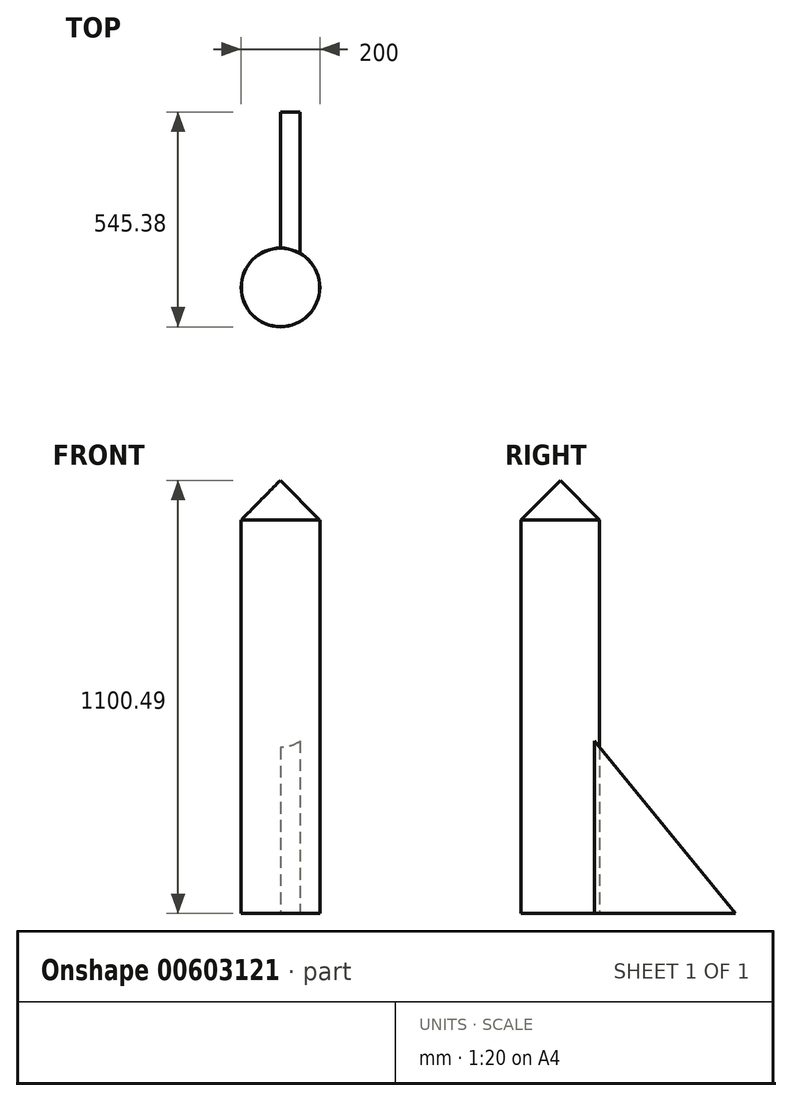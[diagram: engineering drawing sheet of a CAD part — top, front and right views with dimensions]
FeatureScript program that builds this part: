
annotation { "Feature Type Name" : "Feature", "Feature Type Description" : "" }
export const myFeature = defineFeature(function(context is Context, id is Id, definition is map)
    precondition{}
    {
        {
            var Q0;
            Q0=qCreatedBy(makeId("Top.planeOp"),FACE);
            var sketch = newSketch(context, id + "F0", { "sketchPlane" : qUnion([Q0])});
            skCircle(sketch, "E0", {"center": v(0, 0) * mm, "radius": 100 * mm});
            skSolve(sketch);
        }
        {
            var Q0;
            Q0 = qSketchRegion(id + "F0", true);
            extrude(context, id + "F1", {"entities" : qUnion([Q0]), "depth" : 1000 * mm, "offsetDistance" : 25 * mm});
        }
        {
            var Q0;
            Q0=qCreatedBy(makeId("Right.planeOp"),FACE);
            var sketch = newSketch(context, id + "F2", { "sketchPlane" : qUnion([Q0])});
            skLineSegment(sketch, "E1", {"start": v(0, 0) * mm, "end": v(0, 543.34) * mm});
            skLineSegment(sketch, "E2", {"start": v(0, 543.34) * mm, "end": v(445.38, 0) * mm});
            skLineSegment(sketch, "E3", {"start": v(0, 0) * mm, "end": v(445.38, 0) * mm});
            skSolve(sketch);
        }
        {
            var Q0;
            Q0 = qSketchRegion(id + "F2", true);
            extrude(context, id + "F3", {"entities" : qUnion([Q0]), "operationType" : NewBodyOperationType.ADD, "depth" : 50 * mm, "offsetDistance" : 25 * mm});
        }
        {
            var Q0;
            Q0=qCreatedBy(makeId("Front.planeOp"),FACE);
            var sketch = newSketch(context, id + "F4", { "sketchPlane" : qUnion([Q0])});
            skLineSegment(sketch, "E4", {"start": v(-99.45, 1000) * mm, "end": v(0, 1100.49) * mm});
            skLineSegment(sketch, "E5", {"start": v(0, 1100.49) * mm, "end": v(0, 1000.67) * mm});
            skLineSegment(sketch, "E6", {"start": v(0, 1000.67) * mm, "end": v(-99.45, 1000) * mm});
            skSolve(sketch);
        }
        {
            var Q0;
            Q0 = qSketchRegion(id + "F4", true);
            var Q1;
            Q1=makeQuery(id+"F1.opExtrude","CAP_EDGE",EDGE,{"disambiguationData":[OSD([sQuery(id+"F0.wireOp",EDGE,"E0")])],"isStart":false});
            revolve(context, id + "F5", {"entities" : qUnion([Q0]), "axis" : qUnion([Q1]), "revolveType" : RevolveType.FULL});
        }
    });
